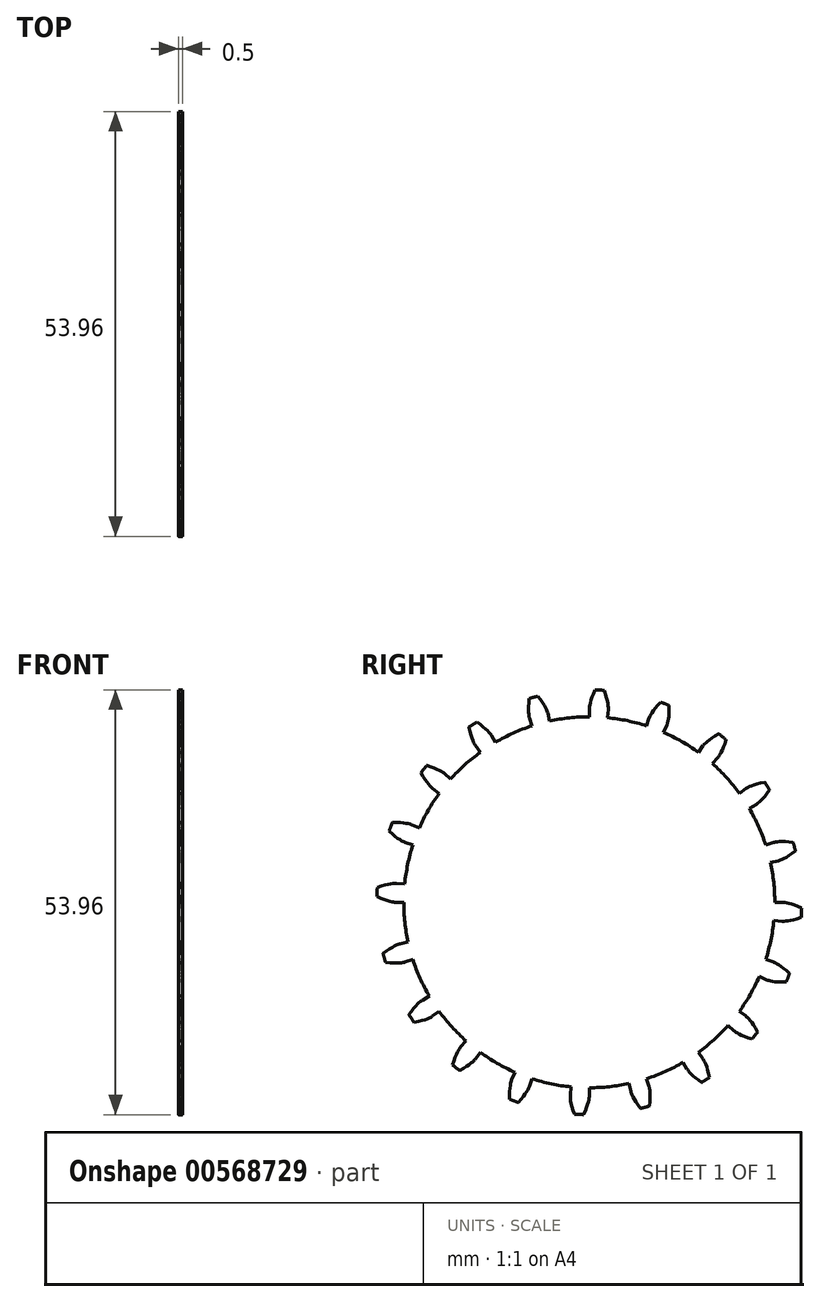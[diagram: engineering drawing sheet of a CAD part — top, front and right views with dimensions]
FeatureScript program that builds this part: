
annotation { "Feature Type Name" : "Feature", "Feature Type Description" : "" }
export const myFeature = defineFeature(function(context is Context, id is Id, definition is map)
    precondition{}
    {
        {
            assignVariable(context, id + "F0", {"name" : "GearThickness", "anyValue" : .5});
        }
        {
            var Q0;
            Q0=qCreatedBy(makeId("Right.planeOp"),FACE);
            var sketch = newSketch(context, id + "F1", { "sketchPlane" : qUnion([Q0])});
            skCircle(sketch, "E0", {"center": v(0, 0) * mm, "radius": 23.56 * mm});
            skCircle(sketch, "E1", {"center": v(0, 0) * mm, "radius": 24.6 * mm, "construction": true});
            skCircle(sketch, "E2", {"center": v(0, 0) * mm, "radius": 25.4 * mm, "construction": true});
            skCircle(sketch, "E3", {"center": v(0, 0) * mm, "radius": 26.99 * mm});
            skLineSegment(sketch, "E4", {"start": v(0, 0) * mm, "end": v(-24.6, 0) * mm, "construction": true});
            skLineSegment(sketch, "E5.1.0", {"start": v(0, 0) * mm, "end": v(-24.56, 1.23) * mm, "construction": true});
            skLineSegment(sketch, "E5.2.0", {"start": v(0, 0) * mm, "end": v(-24.47, 2.45) * mm, "construction": true});
            skLineSegment(sketch, "E5.3.0", {"start": v(0, 0) * mm, "end": v(-24.31, 3.67) * mm, "construction": true});
            skLineSegment(sketch, "E5.4.0", {"start": v(0, 0) * mm, "end": v(-24.1, 4.89) * mm, "construction": true});
            skLineSegment(sketch, "E5.5.0", {"start": v(0, 0) * mm, "end": v(-23.83, 6.08) * mm, "construction": true});
            skLineSegment(sketch, "E5.6.0", {"start": v(0, 0) * mm, "end": v(-23.5, 7.27) * mm, "construction": true});
            skLineSegment(sketch, "E5.7.0", {"start": v(0, 0) * mm, "end": v(-23.1, 8.43) * mm, "construction": true});
            skLineSegment(sketch, "E5.8.0", {"start": v(0, 0) * mm, "end": v(-22.65, 9.58) * mm, "construction": true});
            skLineSegment(sketch, "E5.9.0", {"start": v(0, 0) * mm, "end": v(-22.14, 10.7) * mm, "construction": true});
            skLineSegment(sketch, "E5.10.0", {"start": v(0, 0) * mm, "end": v(-21.58, 11.79) * mm, "construction": true});
            skLineSegment(sketch, "E5.11.0", {"start": v(0, 0) * mm, "end": v(-20.96, 12.85) * mm, "construction": true});
            skLineSegment(sketch, "E5.12.0", {"start": v(0, 0) * mm, "end": v(-20.3, 13.89) * mm, "construction": true});
            skLineSegment(sketch, "E5.13.0", {"start": v(0, 0) * mm, "end": v(-19.58, 14.88) * mm, "construction": true});
            skLineSegment(sketch, "E5.14.0", {"start": v(0, 0) * mm, "end": v(-18.8, 15.84) * mm, "construction": true});
            skLineSegment(sketch, "E5.anchor2", {"start": v(0, 0) * mm, "end": v(-18.8, 15.84) * mm, "construction": true});
            skLineSegment(sketch, "E6", {"start": v(-24.56, 1.23) * mm, "end": v(-24.62, 0) * mm, "construction": true});
            skLineSegment(sketch, "E7", {"start": v(-24.47, 2.45) * mm, "end": v(-24.71, 0) * mm, "construction": true});
            skLineSegment(sketch, "E8", {"start": v(-24.31, 3.67) * mm, "end": v(-24.87, 0.03) * mm, "construction": true});
            skLineSegment(sketch, "E9", {"start": v(-23.83, 6.08) * mm, "end": v(-25.35, 0.13) * mm, "construction": true});
            skLineSegment(sketch, "E10", {"start": v(-23.5, 7.27) * mm, "end": v(-25.67, 0.22) * mm, "construction": true});
            skLineSegment(sketch, "E11", {"start": v(-23.1, 8.43) * mm, "end": v(-26.05, 0.35) * mm, "construction": true});
            skLineSegment(sketch, "E12", {"start": v(-22.65, 9.58) * mm, "end": v(-26.48, 0.52) * mm, "construction": true});
            skLineSegment(sketch, "E13", {"start": v(-22.14, 10.7) * mm, "end": v(-26.96, 0.73) * mm, "construction": true});
            skLineSegment(sketch, "E14", {"start": v(-21.58, 11.79) * mm, "end": v(-27.48, 1) * mm, "construction": true});
            skLineSegment(sketch, "E15", {"start": v(-20.96, 12.85) * mm, "end": v(-28.03, 1.32) * mm, "construction": true});
            skLineSegment(sketch, "E16", {"start": v(-24.1, 4.89) * mm, "end": v(-25.08, 0.07) * mm, "construction": true});
            skLineSegment(sketch, "E17", {"start": v(-20.3, 13.89) * mm, "end": v(-28.63, 1.7) * mm, "construction": true});
            skLineSegment(sketch, "E18", {"start": v(-19.58, 14.88) * mm, "end": v(-29.25, 2.16) * mm, "construction": true});
            skLineSegment(sketch, "E19", {"start": v(-18.8, 15.84) * mm, "end": v(-29.9, 2.68) * mm, "construction": true});
            skLineSegment(sketch, "E20", {"start": v(0, 0) * mm, "end": v(-24.56, 1.2) * mm, "construction": true});
            skLineSegment(sketch, "E21", {"start": v(-23.56, 0) * mm, "end": v(-24.6, 0) * mm});
            skLineSegment(sketch, "E22.MirrorCS", {"start": v(-23.45, 2.3) * mm, "end": v(-24.47, 2.41) * mm});
            skLineSegment(sketch, "E23", {"start": v(-24.6, 0) * mm, "end": v(-24.62, 0) * mm});
            skLineSegment(sketch, "E24", {"start": v(-24.62, 0) * mm, "end": v(-24.71, 0) * mm});
            skLineSegment(sketch, "E25", {"start": v(-24.71, 0) * mm, "end": v(-24.87, 0.03) * mm});
            skLineSegment(sketch, "E26", {"start": v(-24.87, 0.03) * mm, "end": v(-25.08, 0.07) * mm});
            skLineSegment(sketch, "E27", {"start": v(-25.08, 0.07) * mm, "end": v(-25.35, 0.13) * mm});
            skLineSegment(sketch, "E28", {"start": v(-25.35, 0.13) * mm, "end": v(-25.67, 0.22) * mm});
            skLineSegment(sketch, "E29", {"start": v(-25.67, 0.22) * mm, "end": v(-26.05, 0.35) * mm});
            skLineSegment(sketch, "E30", {"start": v(-26.05, 0.35) * mm, "end": v(-26.48, 0.52) * mm});
            skLineSegment(sketch, "E31", {"start": v(-26.48, 0.52) * mm, "end": v(-26.96, 0.73) * mm});
            skLineSegment(sketch, "E32", {"start": v(-26.96, 0.73) * mm, "end": v(-27.48, 1) * mm});
            skLineSegment(sketch, "E33", {"start": v(-27.48, 1) * mm, "end": v(-28.03, 1.32) * mm});
            skLineSegment(sketch, "E34", {"start": v(-28.03, 1.32) * mm, "end": v(-28.63, 1.7) * mm});
            skLineSegment(sketch, "E35", {"start": v(-28.63, 1.7) * mm, "end": v(-29.25, 2.16) * mm});
            skLineSegment(sketch, "E36", {"start": v(-29.25, 2.16) * mm, "end": v(-29.9, 2.68) * mm});
            skLineSegment(sketch, "E37.MirrorCS", {"start": v(-24.47, 2.41) * mm, "end": v(-24.5, 2.41) * mm});
            skLineSegment(sketch, "E38.MirrorCS", {"start": v(-24.5, 2.41) * mm, "end": v(-24.6, 2.41) * mm});
            skLineSegment(sketch, "E39.MirrorCS", {"start": v(-24.6, 2.41) * mm, "end": v(-24.75, 2.4) * mm});
            skLineSegment(sketch, "E40.MirrorCS", {"start": v(-24.75, 2.4) * mm, "end": v(-24.96, 2.4) * mm});
            skLineSegment(sketch, "E41.MirrorCS", {"start": v(-25.24, 2.36) * mm, "end": v(-25.57, 2.3) * mm});
            skLineSegment(sketch, "E42.MirrorCS", {"start": v(-25.57, 2.3) * mm, "end": v(-25.96, 2.2) * mm});
            skLineSegment(sketch, "E43.MirrorCS", {"start": v(-25.96, 2.2) * mm, "end": v(-26.4, 2.08) * mm});
            skLineSegment(sketch, "E44.MirrorCS", {"start": v(-26.4, 2.08) * mm, "end": v(-26.9, 1.91) * mm});
            skLineSegment(sketch, "E45.MirrorCS", {"start": v(-27.44, 1.7) * mm, "end": v(-28.03, 1.43) * mm});
            skLineSegment(sketch, "E46.MirrorCS", {"start": v(-26.9, 1.91) * mm, "end": v(-27.44, 1.7) * mm});
            skLineSegment(sketch, "E47.MirrorCS", {"start": v(-28.03, 1.43) * mm, "end": v(-28.66, 1.1) * mm});
            skLineSegment(sketch, "E48.MirrorCS", {"start": v(-28.66, 1.1) * mm, "end": v(-29.32, 0.72) * mm});
            skLineSegment(sketch, "E49.MirrorCS", {"start": v(-29.32, 0.72) * mm, "end": v(-30.02, 0.27) * mm});
            skLineSegment(sketch, "E50.MirrorCS", {"start": v(-24.96, 2.4) * mm, "end": v(-25.24, 2.36) * mm});
            skLineSegment(sketch, "E51.1.0", {"start": v(-22.4, -7.28) * mm, "end": v(-23.39, -7.6) * mm});
            skLineSegment(sketch, "E51.1.1", {"start": v(-27.1, -7.3) * mm, "end": v(-27.6, -7.8) * mm});
            skLineSegment(sketch, "E51.1.2", {"start": v(-23.02, -5.05) * mm, "end": v(-24.02, -5.27) * mm});
            skLineSegment(sketch, "E51.1.3", {"start": v(-26.62, -6.86) * mm, "end": v(-27.1, -7.3) * mm});
            skLineSegment(sketch, "E51.1.4", {"start": v(-26.44, -7.54) * mm, "end": v(-27.07, -7.4) * mm});
            skLineSegment(sketch, "E51.1.5", {"start": v(-27.07, -7.4) * mm, "end": v(-27.75, -7.22) * mm});
            skLineSegment(sketch, "E51.1.6", {"start": v(-26.17, -6.5) * mm, "end": v(-26.62, -6.86) * mm});
            skLineSegment(sketch, "E51.1.7", {"start": v(-28.1, -8.38) * mm, "end": v(-28.63, -9.02) * mm});
            skLineSegment(sketch, "E51.1.8", {"start": v(-25.75, -6.18) * mm, "end": v(-26.17, -6.5) * mm});
            skLineSegment(sketch, "E51.1.9", {"start": v(-28.48, -6.99) * mm, "end": v(-29.26, -6.7) * mm});
            skLineSegment(sketch, "E51.1.10", {"start": v(-27.6, -7.8) * mm, "end": v(-28.1, -8.38) * mm});
            skLineSegment(sketch, "E51.1.11", {"start": v(-25.86, -7.63) * mm, "end": v(-26.44, -7.54) * mm});
            skLineSegment(sketch, "E51.1.12", {"start": v(-27.75, -7.22) * mm, "end": v(-28.48, -6.99) * mm});
            skLineSegment(sketch, "E51.1.13", {"start": v(-24.73, -5.56) * mm, "end": v(-25.03, -5.72) * mm});
            skLineSegment(sketch, "E51.1.14", {"start": v(-25.03, -5.72) * mm, "end": v(-25.37, -5.92) * mm});
            skLineSegment(sketch, "E51.1.15", {"start": v(-25.37, -5.92) * mm, "end": v(-25.75, -6.18) * mm});
            skLineSegment(sketch, "E51.1.16", {"start": v(-24.88, -7.72) * mm, "end": v(-25.34, -7.7) * mm});
            skLineSegment(sketch, "E51.1.17", {"start": v(-24.48, -7.72) * mm, "end": v(-24.88, -7.72) * mm});
            skLineSegment(sketch, "E51.1.18", {"start": v(-25.34, -7.7) * mm, "end": v(-25.86, -7.63) * mm});
            skLineSegment(sketch, "E51.1.19", {"start": v(-24.48, -5.44) * mm, "end": v(-24.73, -5.56) * mm});
            skLineSegment(sketch, "E51.1.20", {"start": v(-24.28, -5.36) * mm, "end": v(-24.48, -5.44) * mm});
            skLineSegment(sketch, "E51.1.21", {"start": v(-24.15, -7.71) * mm, "end": v(-24.48, -7.72) * mm});
            skLineSegment(sketch, "E51.1.22", {"start": v(-23.87, -7.69) * mm, "end": v(-24.15, -7.71) * mm});
            skLineSegment(sketch, "E51.1.23", {"start": v(-23.5, -7.63) * mm, "end": v(-23.66, -7.66) * mm});
            skLineSegment(sketch, "E51.1.24", {"start": v(-24.02, -5.27) * mm, "end": v(-24.05, -5.28) * mm});
            skLineSegment(sketch, "E51.1.25", {"start": v(-24.05, -5.28) * mm, "end": v(-24.14, -5.3) * mm});
            skLineSegment(sketch, "E51.1.26", {"start": v(-23.66, -7.66) * mm, "end": v(-23.87, -7.69) * mm});
            skLineSegment(sketch, "E51.1.27", {"start": v(-24.14, -5.3) * mm, "end": v(-24.28, -5.36) * mm});
            skLineSegment(sketch, "E51.1.28", {"start": v(-23.42, -7.6) * mm, "end": v(-23.5, -7.63) * mm});
            skLineSegment(sketch, "E51.1.29", {"start": v(-23.39, -7.6) * mm, "end": v(-23.42, -7.6) * mm});
            skLineSegment(sketch, "E51.2.0", {"start": v(-19.06, -13.85) * mm, "end": v(-19.9, -14.45) * mm});
            skLineSegment(sketch, "E51.2.1", {"start": v(-23.52, -15.32) * mm, "end": v(-23.83, -15.95) * mm});
            skLineSegment(sketch, "E51.2.2", {"start": v(-20.33, -11.91) * mm, "end": v(-21.22, -12.43) * mm});
            skLineSegment(sketch, "E51.2.3", {"start": v(-23.2, -14.76) * mm, "end": v(-23.52, -15.32) * mm});
            skLineSegment(sketch, "E51.2.4", {"start": v(-22.82, -15.34) * mm, "end": v(-23.46, -15.4) * mm});
            skLineSegment(sketch, "E51.2.5", {"start": v(-23.46, -15.4) * mm, "end": v(-24.16, -15.44) * mm});
            skLineSegment(sketch, "E51.2.6", {"start": v(-22.89, -14.26) * mm, "end": v(-23.2, -14.76) * mm});
            skLineSegment(sketch, "E51.2.7", {"start": v(-24.14, -16.65) * mm, "end": v(-24.44, -17.43) * mm});
            skLineSegment(sketch, "E51.2.8", {"start": v(-22.58, -13.84) * mm, "end": v(-22.89, -14.26) * mm});
            skLineSegment(sketch, "E51.2.9", {"start": v(-24.93, -15.45) * mm, "end": v(-25.76, -15.4) * mm});
            skLineSegment(sketch, "E51.2.10", {"start": v(-23.83, -15.95) * mm, "end": v(-24.14, -16.65) * mm});
            skLineSegment(sketch, "E51.2.11", {"start": v(-22.24, -15.25) * mm, "end": v(-22.82, -15.34) * mm});
            skLineSegment(sketch, "E51.2.12", {"start": v(-24.16, -15.44) * mm, "end": v(-24.93, -15.45) * mm});
            skLineSegment(sketch, "E51.2.13", {"start": v(-21.8, -12.93) * mm, "end": v(-22.04, -13.17) * mm});
            skLineSegment(sketch, "E51.2.14", {"start": v(-22.04, -13.17) * mm, "end": v(-22.3, -13.47) * mm});
            skLineSegment(sketch, "E51.2.15", {"start": v(-22.3, -13.47) * mm, "end": v(-22.58, -13.84) * mm});
            skLineSegment(sketch, "E51.2.16", {"start": v(-21.28, -15.03) * mm, "end": v(-21.73, -15.15) * mm});
            skLineSegment(sketch, "E51.2.17", {"start": v(-20.9, -14.91) * mm, "end": v(-21.28, -15.03) * mm});
            skLineSegment(sketch, "E51.2.18", {"start": v(-21.73, -15.15) * mm, "end": v(-22.24, -15.25) * mm});
            skLineSegment(sketch, "E51.2.19", {"start": v(-21.6, -12.74) * mm, "end": v(-21.8, -12.93) * mm});
            skLineSegment(sketch, "E51.2.20", {"start": v(-21.44, -12.6) * mm, "end": v(-21.6, -12.74) * mm});
            skLineSegment(sketch, "E51.2.21", {"start": v(-20.58, -14.8) * mm, "end": v(-20.9, -14.91) * mm});
            skLineSegment(sketch, "E51.2.22", {"start": v(-20.33, -14.69) * mm, "end": v(-20.58, -14.8) * mm});
            skLineSegment(sketch, "E51.2.23", {"start": v(-20, -14.52) * mm, "end": v(-20.13, -14.6) * mm});
            skLineSegment(sketch, "E51.2.24", {"start": v(-21.22, -12.43) * mm, "end": v(-21.24, -12.45) * mm});
            skLineSegment(sketch, "E51.2.25", {"start": v(-21.24, -12.45) * mm, "end": v(-21.32, -12.5) * mm});
            skLineSegment(sketch, "E51.2.26", {"start": v(-20.13, -14.6) * mm, "end": v(-20.33, -14.69) * mm});
            skLineSegment(sketch, "E51.2.27", {"start": v(-21.32, -12.5) * mm, "end": v(-21.44, -12.6) * mm});
            skLineSegment(sketch, "E51.2.28", {"start": v(-19.92, -14.47) * mm, "end": v(-20, -14.52) * mm});
            skLineSegment(sketch, "E51.2.29", {"start": v(-19.9, -14.45) * mm, "end": v(-19.92, -14.47) * mm});
            skLineSegment(sketch, "E51.3.0", {"start": v(-13.85, -19.06) * mm, "end": v(-14.45, -19.9) * mm});
            skLineSegment(sketch, "E51.3.1", {"start": v(-17.63, -21.83) * mm, "end": v(-17.74, -22.53) * mm});
            skLineSegment(sketch, "E51.3.2", {"start": v(-15.65, -17.61) * mm, "end": v(-16.33, -18.38) * mm});
            skLineSegment(sketch, "E51.3.3", {"start": v(-17.5, -21.2) * mm, "end": v(-17.63, -21.83) * mm});
            skLineSegment(sketch, "E51.3.4", {"start": v(-16.96, -21.64) * mm, "end": v(-17.55, -21.9) * mm});
            skLineSegment(sketch, "E51.3.5", {"start": v(-17.55, -21.9) * mm, "end": v(-18.2, -22.16) * mm});
            skLineSegment(sketch, "E51.3.6", {"start": v(-17.36, -20.64) * mm, "end": v(-17.5, -21.2) * mm});
            skLineSegment(sketch, "E51.3.7", {"start": v(-17.82, -23.3) * mm, "end": v(-17.86, -24.13) * mm});
            skLineSegment(sketch, "E51.3.8", {"start": v(-17.2, -20.14) * mm, "end": v(-17.36, -20.64) * mm});
            skLineSegment(sketch, "E51.3.9", {"start": v(-18.94, -22.4) * mm, "end": v(-19.74, -22.61) * mm});
            skLineSegment(sketch, "E51.3.10", {"start": v(-17.74, -22.53) * mm, "end": v(-17.82, -23.3) * mm});
            skLineSegment(sketch, "E51.3.11", {"start": v(-16.44, -21.38) * mm, "end": v(-16.96, -21.64) * mm});
            skLineSegment(sketch, "E51.3.12", {"start": v(-18.2, -22.16) * mm, "end": v(-18.94, -22.4) * mm});
            skLineSegment(sketch, "E51.3.13", {"start": v(-16.74, -19.03) * mm, "end": v(-16.89, -19.34) * mm});
            skLineSegment(sketch, "E51.3.14", {"start": v(-16.89, -19.34) * mm, "end": v(-17.05, -19.7) * mm});
            skLineSegment(sketch, "E51.3.15", {"start": v(-17.05, -19.7) * mm, "end": v(-17.2, -20.14) * mm});
            skLineSegment(sketch, "E51.3.16", {"start": v(-15.6, -20.87) * mm, "end": v(-15.98, -21.12) * mm});
            skLineSegment(sketch, "E51.3.17", {"start": v(-15.27, -20.64) * mm, "end": v(-15.6, -20.87) * mm});
            skLineSegment(sketch, "E51.3.18", {"start": v(-15.98, -21.12) * mm, "end": v(-16.44, -21.38) * mm});
            skLineSegment(sketch, "E51.3.19", {"start": v(-16.6, -18.79) * mm, "end": v(-16.74, -19.03) * mm});
            skLineSegment(sketch, "E51.3.20", {"start": v(-16.5, -18.6) * mm, "end": v(-16.6, -18.79) * mm});
            skLineSegment(sketch, "E51.3.21", {"start": v(-15, -20.43) * mm, "end": v(-15.27, -20.64) * mm});
            skLineSegment(sketch, "E51.3.22", {"start": v(-14.8, -20.25) * mm, "end": v(-15, -20.43) * mm});
            skLineSegment(sketch, "E51.3.23", {"start": v(-14.53, -19.99) * mm, "end": v(-14.64, -20.1) * mm});
            skLineSegment(sketch, "E51.3.24", {"start": v(-16.33, -18.38) * mm, "end": v(-16.35, -18.4) * mm});
            skLineSegment(sketch, "E51.3.25", {"start": v(-16.35, -18.4) * mm, "end": v(-16.4, -18.48) * mm});
            skLineSegment(sketch, "E51.3.26", {"start": v(-14.64, -20.1) * mm, "end": v(-14.8, -20.25) * mm});
            skLineSegment(sketch, "E51.3.27", {"start": v(-16.4, -18.48) * mm, "end": v(-16.5, -18.6) * mm});
            skLineSegment(sketch, "E51.3.28", {"start": v(-14.47, -19.92) * mm, "end": v(-14.53, -19.99) * mm});
            skLineSegment(sketch, "E51.3.29", {"start": v(-14.45, -19.9) * mm, "end": v(-14.47, -19.92) * mm});
            skLineSegment(sketch, "E51.4.0", {"start": v(-7.28, -22.4) * mm, "end": v(-7.6, -23.39) * mm});
            skLineSegment(sketch, "E51.4.1", {"start": v(-10.02, -26.21) * mm, "end": v(-9.9, -26.91) * mm});
            skLineSegment(sketch, "E51.4.2", {"start": v(-9.44, -21.59) * mm, "end": v(-9.85, -22.53) * mm});
            skLineSegment(sketch, "E51.4.3", {"start": v(-10.1, -25.57) * mm, "end": v(-10.02, -26.21) * mm});
            skLineSegment(sketch, "E51.4.4", {"start": v(-9.44, -25.82) * mm, "end": v(-9.92, -26.25) * mm});
            skLineSegment(sketch, "E51.4.5", {"start": v(-9.92, -26.25) * mm, "end": v(-10.47, -26.7) * mm});
            skLineSegment(sketch, "E51.4.6", {"start": v(-10.13, -25) * mm, "end": v(-10.1, -25.57) * mm});
            skLineSegment(sketch, "E51.4.7", {"start": v(-9.75, -27.66) * mm, "end": v(-9.53, -28.46) * mm});
            skLineSegment(sketch, "E51.4.8", {"start": v(-10.14, -24.47) * mm, "end": v(-10.13, -25) * mm});
            skLineSegment(sketch, "E51.4.9", {"start": v(-11.1, -27.15) * mm, "end": v(-11.78, -27.6) * mm});
            skLineSegment(sketch, "E51.4.10", {"start": v(-9.9, -26.91) * mm, "end": v(-9.75, -27.66) * mm});
            skLineSegment(sketch, "E51.4.11", {"start": v(-9.03, -25.41) * mm, "end": v(-9.44, -25.82) * mm});
            skLineSegment(sketch, "E51.4.12", {"start": v(-10.47, -26.7) * mm, "end": v(-11.1, -27.15) * mm});
            skLineSegment(sketch, "E51.4.13", {"start": v(-10.04, -23.27) * mm, "end": v(-10.09, -23.6) * mm});
            skLineSegment(sketch, "E51.4.14", {"start": v(-10.09, -23.6) * mm, "end": v(-10.12, -24) * mm});
            skLineSegment(sketch, "E51.4.15", {"start": v(-10.12, -24) * mm, "end": v(-10.14, -24.47) * mm});
            skLineSegment(sketch, "E51.4.16", {"start": v(-8.38, -24.67) * mm, "end": v(-8.67, -25.02) * mm});
            skLineSegment(sketch, "E51.4.17", {"start": v(-8.14, -24.35) * mm, "end": v(-8.38, -24.67) * mm});
            skLineSegment(sketch, "E51.4.18", {"start": v(-8.67, -25.02) * mm, "end": v(-9.03, -25.41) * mm});
            skLineSegment(sketch, "E51.4.19", {"start": v(-10, -23) * mm, "end": v(-10.04, -23.27) * mm});
            skLineSegment(sketch, "E51.4.20", {"start": v(-9.94, -22.8) * mm, "end": v(-10, -23) * mm});
            skLineSegment(sketch, "E51.4.21", {"start": v(-7.95, -24.07) * mm, "end": v(-8.14, -24.35) * mm});
            skLineSegment(sketch, "E51.4.22", {"start": v(-7.81, -23.83) * mm, "end": v(-7.95, -24.07) * mm});
            skLineSegment(sketch, "E51.4.23", {"start": v(-7.64, -23.5) * mm, "end": v(-7.71, -23.64) * mm});
            skLineSegment(sketch, "E51.4.24", {"start": v(-9.85, -22.53) * mm, "end": v(-9.87, -22.56) * mm});
            skLineSegment(sketch, "E51.4.25", {"start": v(-9.87, -22.56) * mm, "end": v(-9.9, -22.65) * mm});
            skLineSegment(sketch, "E51.4.26", {"start": v(-7.71, -23.64) * mm, "end": v(-7.81, -23.83) * mm});
            skLineSegment(sketch, "E51.4.27", {"start": v(-9.9, -22.65) * mm, "end": v(-9.94, -22.8) * mm});
            skLineSegment(sketch, "E51.4.28", {"start": v(-7.6, -23.42) * mm, "end": v(-7.64, -23.5) * mm});
            skLineSegment(sketch, "E51.4.29", {"start": v(-7.6, -23.39) * mm, "end": v(-7.6, -23.42) * mm});
            skLineSegment(sketch, "E51.5.0", {"start": v(0, -23.56) * mm, "end": v(0, -24.6) * mm});
            skLineSegment(sketch, "E51.5.1", {"start": v(-1.43, -28.03) * mm, "end": v(-1.1, -28.66) * mm});
            skLineSegment(sketch, "E51.5.2", {"start": v(-2.3, -23.45) * mm, "end": v(-2.41, -24.47) * mm});
            skLineSegment(sketch, "E51.5.3", {"start": v(-1.7, -27.44) * mm, "end": v(-1.43, -28.03) * mm});
            skLineSegment(sketch, "E51.5.4", {"start": v(-1, -27.48) * mm, "end": v(-1.32, -28.03) * mm});
            skLineSegment(sketch, "E51.5.5", {"start": v(-1.32, -28.03) * mm, "end": v(-1.7, -28.63) * mm});
            skLineSegment(sketch, "E51.5.6", {"start": v(-1.91, -26.9) * mm, "end": v(-1.7, -27.44) * mm});
            skLineSegment(sketch, "E51.5.7", {"start": v(-0.72, -29.32) * mm, "end": v(-0.27, -30.02) * mm});
            skLineSegment(sketch, "E51.5.8", {"start": v(-2.08, -26.4) * mm, "end": v(-1.91, -26.9) * mm});
            skLineSegment(sketch, "E51.5.9", {"start": v(-2.16, -29.25) * mm, "end": v(-2.68, -29.9) * mm});
            skLineSegment(sketch, "E51.5.10", {"start": v(-1.1, -28.66) * mm, "end": v(-0.72, -29.32) * mm});
            skLineSegment(sketch, "E51.5.11", {"start": v(-0.73, -26.96) * mm, "end": v(-1, -27.48) * mm});
            skLineSegment(sketch, "E51.5.12", {"start": v(-1.7, -28.63) * mm, "end": v(-2.16, -29.25) * mm});
            skLineSegment(sketch, "E51.5.13", {"start": v(-2.36, -25.24) * mm, "end": v(-2.3, -25.57) * mm});
            skLineSegment(sketch, "E51.5.14", {"start": v(-2.3, -25.57) * mm, "end": v(-2.2, -25.96) * mm});
            skLineSegment(sketch, "E51.5.15", {"start": v(-2.2, -25.96) * mm, "end": v(-2.08, -26.4) * mm});
            skLineSegment(sketch, "E51.5.16", {"start": v(-0.35, -26.05) * mm, "end": v(-0.52, -26.48) * mm});
            skLineSegment(sketch, "E51.5.17", {"start": v(-0.22, -25.67) * mm, "end": v(-0.35, -26.05) * mm});
            skLineSegment(sketch, "E51.5.18", {"start": v(-0.52, -26.48) * mm, "end": v(-0.73, -26.96) * mm});
            skLineSegment(sketch, "E51.5.19", {"start": v(-2.4, -24.96) * mm, "end": v(-2.36, -25.24) * mm});
            skLineSegment(sketch, "E51.5.20", {"start": v(-2.4, -24.75) * mm, "end": v(-2.4, -24.96) * mm});
            skLineSegment(sketch, "E51.5.21", {"start": v(-0.13, -25.35) * mm, "end": v(-0.22, -25.67) * mm});
            skLineSegment(sketch, "E51.5.22", {"start": v(-0.07, -25.08) * mm, "end": v(-0.13, -25.35) * mm});
            skLineSegment(sketch, "E51.5.23", {"start": v(0, -24.71) * mm, "end": v(-0.03, -24.87) * mm});
            skLineSegment(sketch, "E51.5.24", {"start": v(-2.41, -24.47) * mm, "end": v(-2.41, -24.5) * mm});
            skLineSegment(sketch, "E51.5.25", {"start": v(-2.41, -24.5) * mm, "end": v(-2.41, -24.6) * mm});
            skLineSegment(sketch, "E51.5.26", {"start": v(-0.03, -24.87) * mm, "end": v(-0.07, -25.08) * mm});
            skLineSegment(sketch, "E51.5.27", {"start": v(-2.41, -24.6) * mm, "end": v(-2.4, -24.75) * mm});
            skLineSegment(sketch, "E51.5.28", {"start": v(0, -24.62) * mm, "end": v(0, -24.71) * mm});
            skLineSegment(sketch, "E51.5.29", {"start": v(0, -24.6) * mm, "end": v(0, -24.62) * mm});
            skLineSegment(sketch, "E51.6.0", {"start": v(7.28, -22.4) * mm, "end": v(7.6, -23.39) * mm});
            skLineSegment(sketch, "E51.6.1", {"start": v(7.3, -27.1) * mm, "end": v(7.8, -27.6) * mm});
            skLineSegment(sketch, "E51.6.2", {"start": v(5.05, -23.02) * mm, "end": v(5.27, -24.02) * mm});
            skLineSegment(sketch, "E51.6.3", {"start": v(6.86, -26.62) * mm, "end": v(7.3, -27.1) * mm});
            skLineSegment(sketch, "E51.6.4", {"start": v(7.54, -26.44) * mm, "end": v(7.4, -27.07) * mm});
            skLineSegment(sketch, "E51.6.5", {"start": v(7.4, -27.07) * mm, "end": v(7.22, -27.75) * mm});
            skLineSegment(sketch, "E51.6.6", {"start": v(6.5, -26.17) * mm, "end": v(6.86, -26.62) * mm});
            skLineSegment(sketch, "E51.6.7", {"start": v(8.38, -28.1) * mm, "end": v(9.02, -28.63) * mm});
            skLineSegment(sketch, "E51.6.8", {"start": v(6.18, -25.75) * mm, "end": v(6.5, -26.17) * mm});
            skLineSegment(sketch, "E51.6.9", {"start": v(6.99, -28.48) * mm, "end": v(6.7, -29.26) * mm});
            skLineSegment(sketch, "E51.6.10", {"start": v(7.8, -27.6) * mm, "end": v(8.38, -28.1) * mm});
            skLineSegment(sketch, "E51.6.11", {"start": v(7.63, -25.86) * mm, "end": v(7.54, -26.44) * mm});
            skLineSegment(sketch, "E51.6.12", {"start": v(7.22, -27.75) * mm, "end": v(6.99, -28.48) * mm});
            skLineSegment(sketch, "E51.6.13", {"start": v(5.56, -24.73) * mm, "end": v(5.72, -25.03) * mm});
            skLineSegment(sketch, "E51.6.14", {"start": v(5.72, -25.03) * mm, "end": v(5.92, -25.37) * mm});
            skLineSegment(sketch, "E51.6.15", {"start": v(5.92, -25.37) * mm, "end": v(6.18, -25.75) * mm});
            skLineSegment(sketch, "E51.6.16", {"start": v(7.72, -24.88) * mm, "end": v(7.7, -25.34) * mm});
            skLineSegment(sketch, "E51.6.17", {"start": v(7.72, -24.48) * mm, "end": v(7.72, -24.88) * mm});
            skLineSegment(sketch, "E51.6.18", {"start": v(7.7, -25.34) * mm, "end": v(7.63, -25.86) * mm});
            skLineSegment(sketch, "E51.6.19", {"start": v(5.44, -24.48) * mm, "end": v(5.56, -24.73) * mm});
            skLineSegment(sketch, "E51.6.20", {"start": v(5.36, -24.28) * mm, "end": v(5.44, -24.48) * mm});
            skLineSegment(sketch, "E51.6.21", {"start": v(7.71, -24.15) * mm, "end": v(7.72, -24.48) * mm});
            skLineSegment(sketch, "E51.6.22", {"start": v(7.69, -23.87) * mm, "end": v(7.71, -24.15) * mm});
            skLineSegment(sketch, "E51.6.23", {"start": v(7.63, -23.5) * mm, "end": v(7.66, -23.66) * mm});
            skLineSegment(sketch, "E51.6.24", {"start": v(5.27, -24.02) * mm, "end": v(5.28, -24.05) * mm});
            skLineSegment(sketch, "E51.6.25", {"start": v(5.28, -24.05) * mm, "end": v(5.3, -24.14) * mm});
            skLineSegment(sketch, "E51.6.26", {"start": v(7.66, -23.66) * mm, "end": v(7.69, -23.87) * mm});
            skLineSegment(sketch, "E51.6.27", {"start": v(5.3, -24.14) * mm, "end": v(5.36, -24.28) * mm});
            skLineSegment(sketch, "E51.6.28", {"start": v(7.6, -23.42) * mm, "end": v(7.63, -23.5) * mm});
            skLineSegment(sketch, "E51.6.29", {"start": v(7.6, -23.39) * mm, "end": v(7.6, -23.42) * mm});
            skLineSegment(sketch, "E51.7.0", {"start": v(13.85, -19.06) * mm, "end": v(14.45, -19.9) * mm});
            skLineSegment(sketch, "E51.7.1", {"start": v(15.32, -23.52) * mm, "end": v(15.95, -23.83) * mm});
            skLineSegment(sketch, "E51.7.2", {"start": v(11.91, -20.33) * mm, "end": v(12.43, -21.22) * mm});
            skLineSegment(sketch, "E51.7.3", {"start": v(14.76, -23.2) * mm, "end": v(15.32, -23.52) * mm});
            skLineSegment(sketch, "E51.7.4", {"start": v(15.34, -22.82) * mm, "end": v(15.4, -23.46) * mm});
            skLineSegment(sketch, "E51.7.5", {"start": v(15.4, -23.46) * mm, "end": v(15.44, -24.16) * mm});
            skLineSegment(sketch, "E51.7.6", {"start": v(14.26, -22.89) * mm, "end": v(14.76, -23.2) * mm});
            skLineSegment(sketch, "E51.7.7", {"start": v(16.65, -24.14) * mm, "end": v(17.43, -24.44) * mm});
            skLineSegment(sketch, "E51.7.8", {"start": v(13.84, -22.58) * mm, "end": v(14.26, -22.89) * mm});
            skLineSegment(sketch, "E51.7.9", {"start": v(15.45, -24.93) * mm, "end": v(15.4, -25.76) * mm});
            skLineSegment(sketch, "E51.7.10", {"start": v(15.95, -23.83) * mm, "end": v(16.65, -24.14) * mm});
            skLineSegment(sketch, "E51.7.11", {"start": v(15.25, -22.24) * mm, "end": v(15.34, -22.82) * mm});
            skLineSegment(sketch, "E51.7.12", {"start": v(15.44, -24.16) * mm, "end": v(15.45, -24.93) * mm});
            skLineSegment(sketch, "E51.7.13", {"start": v(12.93, -21.8) * mm, "end": v(13.17, -22.04) * mm});
            skLineSegment(sketch, "E51.7.14", {"start": v(13.17, -22.04) * mm, "end": v(13.47, -22.3) * mm});
            skLineSegment(sketch, "E51.7.15", {"start": v(13.47, -22.3) * mm, "end": v(13.84, -22.58) * mm});
            skLineSegment(sketch, "E51.7.16", {"start": v(15.03, -21.28) * mm, "end": v(15.15, -21.73) * mm});
            skLineSegment(sketch, "E51.7.17", {"start": v(14.91, -20.9) * mm, "end": v(15.03, -21.28) * mm});
            skLineSegment(sketch, "E51.7.18", {"start": v(15.15, -21.73) * mm, "end": v(15.25, -22.24) * mm});
            skLineSegment(sketch, "E51.7.19", {"start": v(12.74, -21.6) * mm, "end": v(12.93, -21.8) * mm});
            skLineSegment(sketch, "E51.7.20", {"start": v(12.6, -21.44) * mm, "end": v(12.74, -21.6) * mm});
            skLineSegment(sketch, "E51.7.21", {"start": v(14.8, -20.58) * mm, "end": v(14.91, -20.9) * mm});
            skLineSegment(sketch, "E51.7.22", {"start": v(14.69, -20.33) * mm, "end": v(14.8, -20.58) * mm});
            skLineSegment(sketch, "E51.7.23", {"start": v(14.52, -20) * mm, "end": v(14.6, -20.13) * mm});
            skLineSegment(sketch, "E51.7.24", {"start": v(12.43, -21.22) * mm, "end": v(12.45, -21.24) * mm});
            skLineSegment(sketch, "E51.7.25", {"start": v(12.45, -21.24) * mm, "end": v(12.5, -21.32) * mm});
            skLineSegment(sketch, "E51.7.26", {"start": v(14.6, -20.13) * mm, "end": v(14.69, -20.33) * mm});
            skLineSegment(sketch, "E51.7.27", {"start": v(12.5, -21.32) * mm, "end": v(12.6, -21.44) * mm});
            skLineSegment(sketch, "E51.7.28", {"start": v(14.47, -19.92) * mm, "end": v(14.52, -20) * mm});
            skLineSegment(sketch, "E51.7.29", {"start": v(14.45, -19.9) * mm, "end": v(14.47, -19.92) * mm});
            skLineSegment(sketch, "E51.8.0", {"start": v(19.06, -13.85) * mm, "end": v(19.9, -14.45) * mm});
            skLineSegment(sketch, "E51.8.1", {"start": v(21.83, -17.63) * mm, "end": v(22.53, -17.74) * mm});
            skLineSegment(sketch, "E51.8.2", {"start": v(17.61, -15.65) * mm, "end": v(18.38, -16.33) * mm});
            skLineSegment(sketch, "E51.8.3", {"start": v(21.2, -17.5) * mm, "end": v(21.83, -17.63) * mm});
            skLineSegment(sketch, "E51.8.4", {"start": v(21.64, -16.96) * mm, "end": v(21.9, -17.55) * mm});
            skLineSegment(sketch, "E51.8.5", {"start": v(21.9, -17.55) * mm, "end": v(22.16, -18.2) * mm});
            skLineSegment(sketch, "E51.8.6", {"start": v(20.64, -17.36) * mm, "end": v(21.2, -17.5) * mm});
            skLineSegment(sketch, "E51.8.7", {"start": v(23.3, -17.82) * mm, "end": v(24.13, -17.86) * mm});
            skLineSegment(sketch, "E51.8.8", {"start": v(20.14, -17.2) * mm, "end": v(20.64, -17.36) * mm});
            skLineSegment(sketch, "E51.8.9", {"start": v(22.4, -18.94) * mm, "end": v(22.61, -19.74) * mm});
            skLineSegment(sketch, "E51.8.10", {"start": v(22.53, -17.74) * mm, "end": v(23.3, -17.82) * mm});
            skLineSegment(sketch, "E51.8.11", {"start": v(21.38, -16.44) * mm, "end": v(21.64, -16.96) * mm});
            skLineSegment(sketch, "E51.8.12", {"start": v(22.16, -18.2) * mm, "end": v(22.4, -18.94) * mm});
            skLineSegment(sketch, "E51.8.13", {"start": v(19.03, -16.74) * mm, "end": v(19.34, -16.89) * mm});
            skLineSegment(sketch, "E51.8.14", {"start": v(19.34, -16.89) * mm, "end": v(19.7, -17.05) * mm});
            skLineSegment(sketch, "E51.8.15", {"start": v(19.7, -17.05) * mm, "end": v(20.14, -17.2) * mm});
            skLineSegment(sketch, "E51.8.16", {"start": v(20.87, -15.6) * mm, "end": v(21.12, -15.98) * mm});
            skLineSegment(sketch, "E51.8.17", {"start": v(20.64, -15.27) * mm, "end": v(20.87, -15.6) * mm});
            skLineSegment(sketch, "E51.8.18", {"start": v(21.12, -15.98) * mm, "end": v(21.38, -16.44) * mm});
            skLineSegment(sketch, "E51.8.19", {"start": v(18.79, -16.6) * mm, "end": v(19.03, -16.74) * mm});
            skLineSegment(sketch, "E51.8.20", {"start": v(18.6, -16.5) * mm, "end": v(18.79, -16.6) * mm});
            skLineSegment(sketch, "E51.8.21", {"start": v(20.43, -15) * mm, "end": v(20.64, -15.27) * mm});
            skLineSegment(sketch, "E51.8.22", {"start": v(20.25, -14.8) * mm, "end": v(20.43, -15) * mm});
            skLineSegment(sketch, "E51.8.23", {"start": v(19.99, -14.53) * mm, "end": v(20.1, -14.64) * mm});
            skLineSegment(sketch, "E51.8.24", {"start": v(18.38, -16.33) * mm, "end": v(18.4, -16.35) * mm});
            skLineSegment(sketch, "E51.8.25", {"start": v(18.4, -16.35) * mm, "end": v(18.48, -16.4) * mm});
            skLineSegment(sketch, "E51.8.26", {"start": v(20.1, -14.64) * mm, "end": v(20.25, -14.8) * mm});
            skLineSegment(sketch, "E51.8.27", {"start": v(18.48, -16.4) * mm, "end": v(18.6, -16.5) * mm});
            skLineSegment(sketch, "E51.8.28", {"start": v(19.92, -14.47) * mm, "end": v(19.99, -14.53) * mm});
            skLineSegment(sketch, "E51.8.29", {"start": v(19.9, -14.45) * mm, "end": v(19.92, -14.47) * mm});
            skLineSegment(sketch, "E51.9.0", {"start": v(22.4, -7.28) * mm, "end": v(23.39, -7.6) * mm});
            skLineSegment(sketch, "E51.9.1", {"start": v(26.21, -10.02) * mm, "end": v(26.91, -9.9) * mm});
            skLineSegment(sketch, "E51.9.2", {"start": v(21.59, -9.44) * mm, "end": v(22.53, -9.85) * mm});
            skLineSegment(sketch, "E51.9.3", {"start": v(25.57, -10.1) * mm, "end": v(26.21, -10.02) * mm});
            skLineSegment(sketch, "E51.9.4", {"start": v(25.82, -9.44) * mm, "end": v(26.25, -9.92) * mm});
            skLineSegment(sketch, "E51.9.5", {"start": v(26.25, -9.92) * mm, "end": v(26.7, -10.47) * mm});
            skLineSegment(sketch, "E51.9.6", {"start": v(25, -10.13) * mm, "end": v(25.57, -10.1) * mm});
            skLineSegment(sketch, "E51.9.7", {"start": v(27.66, -9.75) * mm, "end": v(28.46, -9.53) * mm});
            skLineSegment(sketch, "E51.9.8", {"start": v(24.47, -10.14) * mm, "end": v(25, -10.13) * mm});
            skLineSegment(sketch, "E51.9.9", {"start": v(27.15, -11.1) * mm, "end": v(27.6, -11.78) * mm});
            skLineSegment(sketch, "E51.9.10", {"start": v(26.91, -9.9) * mm, "end": v(27.66, -9.75) * mm});
            skLineSegment(sketch, "E51.9.11", {"start": v(25.41, -9.03) * mm, "end": v(25.82, -9.44) * mm});
            skLineSegment(sketch, "E51.9.12", {"start": v(26.7, -10.47) * mm, "end": v(27.15, -11.1) * mm});
            skLineSegment(sketch, "E51.9.13", {"start": v(23.27, -10.04) * mm, "end": v(23.6, -10.09) * mm});
            skLineSegment(sketch, "E51.9.14", {"start": v(23.6, -10.09) * mm, "end": v(24, -10.12) * mm});
            skLineSegment(sketch, "E51.9.15", {"start": v(24, -10.12) * mm, "end": v(24.47, -10.14) * mm});
            skLineSegment(sketch, "E51.9.16", {"start": v(24.67, -8.38) * mm, "end": v(25.02, -8.67) * mm});
            skLineSegment(sketch, "E51.9.17", {"start": v(24.35, -8.14) * mm, "end": v(24.67, -8.38) * mm});
            skLineSegment(sketch, "E51.9.18", {"start": v(25.02, -8.67) * mm, "end": v(25.41, -9.03) * mm});
            skLineSegment(sketch, "E51.9.19", {"start": v(23, -10) * mm, "end": v(23.27, -10.04) * mm});
            skLineSegment(sketch, "E51.9.20", {"start": v(22.8, -9.94) * mm, "end": v(23, -10) * mm});
            skLineSegment(sketch, "E51.9.21", {"start": v(24.07, -7.95) * mm, "end": v(24.35, -8.14) * mm});
            skLineSegment(sketch, "E51.9.22", {"start": v(23.83, -7.81) * mm, "end": v(24.07, -7.95) * mm});
            skLineSegment(sketch, "E51.9.23", {"start": v(23.5, -7.64) * mm, "end": v(23.64, -7.71) * mm});
            skLineSegment(sketch, "E51.9.24", {"start": v(22.53, -9.85) * mm, "end": v(22.56, -9.87) * mm});
            skLineSegment(sketch, "E51.9.25", {"start": v(22.56, -9.87) * mm, "end": v(22.65, -9.9) * mm});
            skLineSegment(sketch, "E51.9.26", {"start": v(23.64, -7.71) * mm, "end": v(23.83, -7.81) * mm});
            skLineSegment(sketch, "E51.9.27", {"start": v(22.65, -9.9) * mm, "end": v(22.8, -9.94) * mm});
            skLineSegment(sketch, "E51.9.28", {"start": v(23.42, -7.6) * mm, "end": v(23.5, -7.64) * mm});
            skLineSegment(sketch, "E51.9.29", {"start": v(23.39, -7.6) * mm, "end": v(23.42, -7.6) * mm});
            skLineSegment(sketch, "E51.10.0", {"start": v(23.56, 0) * mm, "end": v(24.6, 0) * mm});
            skLineSegment(sketch, "E51.10.1", {"start": v(28.03, -1.43) * mm, "end": v(28.66, -1.1) * mm});
            skLineSegment(sketch, "E51.10.2", {"start": v(23.45, -2.3) * mm, "end": v(24.47, -2.41) * mm});
            skLineSegment(sketch, "E51.10.3", {"start": v(27.44, -1.7) * mm, "end": v(28.03, -1.43) * mm});
            skLineSegment(sketch, "E51.10.4", {"start": v(27.48, -1) * mm, "end": v(28.03, -1.32) * mm});
            skLineSegment(sketch, "E51.10.5", {"start": v(28.03, -1.32) * mm, "end": v(28.63, -1.7) * mm});
            skLineSegment(sketch, "E51.10.6", {"start": v(26.9, -1.91) * mm, "end": v(27.44, -1.7) * mm});
            skLineSegment(sketch, "E51.10.7", {"start": v(29.32, -0.72) * mm, "end": v(30.02, -0.27) * mm});
            skLineSegment(sketch, "E51.10.8", {"start": v(26.4, -2.08) * mm, "end": v(26.9, -1.91) * mm});
            skLineSegment(sketch, "E51.10.9", {"start": v(29.25, -2.16) * mm, "end": v(29.9, -2.68) * mm});
            skLineSegment(sketch, "E51.10.10", {"start": v(28.66, -1.1) * mm, "end": v(29.32, -0.72) * mm});
            skLineSegment(sketch, "E51.10.11", {"start": v(26.96, -0.73) * mm, "end": v(27.48, -1) * mm});
            skLineSegment(sketch, "E51.10.12", {"start": v(28.63, -1.7) * mm, "end": v(29.25, -2.16) * mm});
            skLineSegment(sketch, "E51.10.13", {"start": v(25.24, -2.36) * mm, "end": v(25.57, -2.3) * mm});
            skLineSegment(sketch, "E51.10.14", {"start": v(25.57, -2.3) * mm, "end": v(25.96, -2.2) * mm});
            skLineSegment(sketch, "E51.10.15", {"start": v(25.96, -2.2) * mm, "end": v(26.4, -2.08) * mm});
            skLineSegment(sketch, "E51.10.16", {"start": v(26.05, -0.35) * mm, "end": v(26.48, -0.52) * mm});
            skLineSegment(sketch, "E51.10.17", {"start": v(25.67, -0.22) * mm, "end": v(26.05, -0.35) * mm});
            skLineSegment(sketch, "E51.10.18", {"start": v(26.48, -0.52) * mm, "end": v(26.96, -0.73) * mm});
            skLineSegment(sketch, "E51.10.19", {"start": v(24.96, -2.4) * mm, "end": v(25.24, -2.36) * mm});
            skLineSegment(sketch, "E51.10.20", {"start": v(24.75, -2.4) * mm, "end": v(24.96, -2.4) * mm});
            skLineSegment(sketch, "E51.10.21", {"start": v(25.35, -0.13) * mm, "end": v(25.67, -0.22) * mm});
            skLineSegment(sketch, "E51.10.22", {"start": v(25.08, -0.07) * mm, "end": v(25.35, -0.13) * mm});
            skLineSegment(sketch, "E51.10.23", {"start": v(24.71, 0) * mm, "end": v(24.87, -0.03) * mm});
            skLineSegment(sketch, "E51.10.24", {"start": v(24.47, -2.41) * mm, "end": v(24.5, -2.41) * mm});
            skLineSegment(sketch, "E51.10.25", {"start": v(24.5, -2.41) * mm, "end": v(24.6, -2.41) * mm});
            skLineSegment(sketch, "E51.10.26", {"start": v(24.87, -0.03) * mm, "end": v(25.08, -0.07) * mm});
            skLineSegment(sketch, "E51.10.27", {"start": v(24.6, -2.41) * mm, "end": v(24.75, -2.4) * mm});
            skLineSegment(sketch, "E51.10.28", {"start": v(24.62, 0) * mm, "end": v(24.71, 0) * mm});
            skLineSegment(sketch, "E51.10.29", {"start": v(24.6, 0) * mm, "end": v(24.62, 0) * mm});
            skLineSegment(sketch, "E51.11.0", {"start": v(22.4, 7.28) * mm, "end": v(23.39, 7.6) * mm});
            skLineSegment(sketch, "E51.11.1", {"start": v(27.1, 7.3) * mm, "end": v(27.6, 7.8) * mm});
            skLineSegment(sketch, "E51.11.2", {"start": v(23.02, 5.05) * mm, "end": v(24.02, 5.27) * mm});
            skLineSegment(sketch, "E51.11.3", {"start": v(26.62, 6.86) * mm, "end": v(27.1, 7.3) * mm});
            skLineSegment(sketch, "E51.11.4", {"start": v(26.44, 7.54) * mm, "end": v(27.07, 7.4) * mm});
            skLineSegment(sketch, "E51.11.5", {"start": v(27.07, 7.4) * mm, "end": v(27.75, 7.22) * mm});
            skLineSegment(sketch, "E51.11.6", {"start": v(26.17, 6.5) * mm, "end": v(26.62, 6.86) * mm});
            skLineSegment(sketch, "E51.11.7", {"start": v(28.1, 8.38) * mm, "end": v(28.63, 9.02) * mm});
            skLineSegment(sketch, "E51.11.8", {"start": v(25.75, 6.18) * mm, "end": v(26.17, 6.5) * mm});
            skLineSegment(sketch, "E51.11.9", {"start": v(28.48, 6.99) * mm, "end": v(29.26, 6.7) * mm});
            skLineSegment(sketch, "E51.11.10", {"start": v(27.6, 7.8) * mm, "end": v(28.1, 8.38) * mm});
            skLineSegment(sketch, "E51.11.11", {"start": v(25.86, 7.63) * mm, "end": v(26.44, 7.54) * mm});
            skLineSegment(sketch, "E51.11.12", {"start": v(27.75, 7.22) * mm, "end": v(28.48, 6.99) * mm});
            skLineSegment(sketch, "E51.11.13", {"start": v(24.73, 5.56) * mm, "end": v(25.03, 5.72) * mm});
            skLineSegment(sketch, "E51.11.14", {"start": v(25.03, 5.72) * mm, "end": v(25.37, 5.92) * mm});
            skLineSegment(sketch, "E51.11.15", {"start": v(25.37, 5.92) * mm, "end": v(25.75, 6.18) * mm});
            skLineSegment(sketch, "E51.11.16", {"start": v(24.88, 7.72) * mm, "end": v(25.34, 7.7) * mm});
            skLineSegment(sketch, "E51.11.17", {"start": v(24.48, 7.72) * mm, "end": v(24.88, 7.72) * mm});
            skLineSegment(sketch, "E51.11.18", {"start": v(25.34, 7.7) * mm, "end": v(25.86, 7.63) * mm});
            skLineSegment(sketch, "E51.11.19", {"start": v(24.48, 5.44) * mm, "end": v(24.73, 5.56) * mm});
            skLineSegment(sketch, "E51.11.20", {"start": v(24.28, 5.36) * mm, "end": v(24.48, 5.44) * mm});
            skLineSegment(sketch, "E51.11.21", {"start": v(24.15, 7.71) * mm, "end": v(24.48, 7.72) * mm});
            skLineSegment(sketch, "E51.11.22", {"start": v(23.87, 7.69) * mm, "end": v(24.15, 7.71) * mm});
            skLineSegment(sketch, "E51.11.23", {"start": v(23.5, 7.63) * mm, "end": v(23.66, 7.66) * mm});
            skLineSegment(sketch, "E51.11.24", {"start": v(24.02, 5.27) * mm, "end": v(24.05, 5.28) * mm});
            skLineSegment(sketch, "E51.11.25", {"start": v(24.05, 5.28) * mm, "end": v(24.14, 5.3) * mm});
            skLineSegment(sketch, "E51.11.26", {"start": v(23.66, 7.66) * mm, "end": v(23.87, 7.69) * mm});
            skLineSegment(sketch, "E51.11.27", {"start": v(24.14, 5.3) * mm, "end": v(24.28, 5.36) * mm});
            skLineSegment(sketch, "E51.11.28", {"start": v(23.42, 7.6) * mm, "end": v(23.5, 7.63) * mm});
            skLineSegment(sketch, "E51.11.29", {"start": v(23.39, 7.6) * mm, "end": v(23.42, 7.6) * mm});
            skLineSegment(sketch, "E51.12.0", {"start": v(19.06, 13.85) * mm, "end": v(19.9, 14.45) * mm});
            skLineSegment(sketch, "E51.12.1", {"start": v(23.52, 15.32) * mm, "end": v(23.83, 15.95) * mm});
            skLineSegment(sketch, "E51.12.2", {"start": v(20.33, 11.91) * mm, "end": v(21.22, 12.43) * mm});
            skLineSegment(sketch, "E51.12.3", {"start": v(23.2, 14.76) * mm, "end": v(23.52, 15.32) * mm});
            skLineSegment(sketch, "E51.12.4", {"start": v(22.82, 15.34) * mm, "end": v(23.46, 15.4) * mm});
            skLineSegment(sketch, "E51.12.5", {"start": v(23.46, 15.4) * mm, "end": v(24.16, 15.44) * mm});
            skLineSegment(sketch, "E51.12.6", {"start": v(22.89, 14.26) * mm, "end": v(23.2, 14.76) * mm});
            skLineSegment(sketch, "E51.12.7", {"start": v(24.14, 16.65) * mm, "end": v(24.44, 17.43) * mm});
            skLineSegment(sketch, "E51.12.8", {"start": v(22.58, 13.84) * mm, "end": v(22.89, 14.26) * mm});
            skLineSegment(sketch, "E51.12.9", {"start": v(24.93, 15.45) * mm, "end": v(25.76, 15.4) * mm});
            skLineSegment(sketch, "E51.12.10", {"start": v(23.83, 15.95) * mm, "end": v(24.14, 16.65) * mm});
            skLineSegment(sketch, "E51.12.11", {"start": v(22.24, 15.25) * mm, "end": v(22.82, 15.34) * mm});
            skLineSegment(sketch, "E51.12.12", {"start": v(24.16, 15.44) * mm, "end": v(24.93, 15.45) * mm});
            skLineSegment(sketch, "E51.12.13", {"start": v(21.8, 12.93) * mm, "end": v(22.04, 13.17) * mm});
            skLineSegment(sketch, "E51.12.14", {"start": v(22.04, 13.17) * mm, "end": v(22.3, 13.47) * mm});
            skLineSegment(sketch, "E51.12.15", {"start": v(22.3, 13.47) * mm, "end": v(22.58, 13.84) * mm});
            skLineSegment(sketch, "E51.12.16", {"start": v(21.28, 15.03) * mm, "end": v(21.73, 15.15) * mm});
            skLineSegment(sketch, "E51.12.17", {"start": v(20.9, 14.91) * mm, "end": v(21.28, 15.03) * mm});
            skLineSegment(sketch, "E51.12.18", {"start": v(21.73, 15.15) * mm, "end": v(22.24, 15.25) * mm});
            skLineSegment(sketch, "E51.12.19", {"start": v(21.6, 12.74) * mm, "end": v(21.8, 12.93) * mm});
            skLineSegment(sketch, "E51.12.20", {"start": v(21.44, 12.6) * mm, "end": v(21.6, 12.74) * mm});
            skLineSegment(sketch, "E51.12.21", {"start": v(20.58, 14.8) * mm, "end": v(20.9, 14.91) * mm});
            skLineSegment(sketch, "E51.12.22", {"start": v(20.33, 14.69) * mm, "end": v(20.58, 14.8) * mm});
            skLineSegment(sketch, "E51.12.23", {"start": v(20, 14.52) * mm, "end": v(20.13, 14.6) * mm});
            skLineSegment(sketch, "E51.12.24", {"start": v(21.22, 12.43) * mm, "end": v(21.24, 12.45) * mm});
            skLineSegment(sketch, "E51.12.25", {"start": v(21.24, 12.45) * mm, "end": v(21.32, 12.5) * mm});
            skLineSegment(sketch, "E51.12.26", {"start": v(20.13, 14.6) * mm, "end": v(20.33, 14.69) * mm});
            skLineSegment(sketch, "E51.12.27", {"start": v(21.32, 12.5) * mm, "end": v(21.44, 12.6) * mm});
            skLineSegment(sketch, "E51.12.28", {"start": v(19.92, 14.47) * mm, "end": v(20, 14.52) * mm});
            skLineSegment(sketch, "E51.12.29", {"start": v(19.9, 14.45) * mm, "end": v(19.92, 14.47) * mm});
            skLineSegment(sketch, "E51.13.0", {"start": v(13.85, 19.06) * mm, "end": v(14.45, 19.9) * mm});
            skLineSegment(sketch, "E51.13.1", {"start": v(17.63, 21.83) * mm, "end": v(17.74, 22.53) * mm});
            skLineSegment(sketch, "E51.13.2", {"start": v(15.65, 17.61) * mm, "end": v(16.33, 18.38) * mm});
            skLineSegment(sketch, "E51.13.3", {"start": v(17.5, 21.2) * mm, "end": v(17.63, 21.83) * mm});
            skLineSegment(sketch, "E51.13.4", {"start": v(16.96, 21.64) * mm, "end": v(17.55, 21.9) * mm});
            skLineSegment(sketch, "E51.13.5", {"start": v(17.55, 21.9) * mm, "end": v(18.2, 22.16) * mm});
            skLineSegment(sketch, "E51.13.6", {"start": v(17.36, 20.64) * mm, "end": v(17.5, 21.2) * mm});
            skLineSegment(sketch, "E51.13.7", {"start": v(17.82, 23.3) * mm, "end": v(17.86, 24.13) * mm});
            skLineSegment(sketch, "E51.13.8", {"start": v(17.2, 20.14) * mm, "end": v(17.36, 20.64) * mm});
            skLineSegment(sketch, "E51.13.9", {"start": v(18.94, 22.4) * mm, "end": v(19.74, 22.61) * mm});
            skLineSegment(sketch, "E51.13.10", {"start": v(17.74, 22.53) * mm, "end": v(17.82, 23.3) * mm});
            skLineSegment(sketch, "E51.13.11", {"start": v(16.44, 21.38) * mm, "end": v(16.96, 21.64) * mm});
            skLineSegment(sketch, "E51.13.12", {"start": v(18.2, 22.16) * mm, "end": v(18.94, 22.4) * mm});
            skLineSegment(sketch, "E51.13.13", {"start": v(16.74, 19.03) * mm, "end": v(16.89, 19.34) * mm});
            skLineSegment(sketch, "E51.13.14", {"start": v(16.89, 19.34) * mm, "end": v(17.05, 19.7) * mm});
            skLineSegment(sketch, "E51.13.15", {"start": v(17.05, 19.7) * mm, "end": v(17.2, 20.14) * mm});
            skLineSegment(sketch, "E51.13.16", {"start": v(15.6, 20.87) * mm, "end": v(15.98, 21.12) * mm});
            skLineSegment(sketch, "E51.13.17", {"start": v(15.27, 20.64) * mm, "end": v(15.6, 20.87) * mm});
            skLineSegment(sketch, "E51.13.18", {"start": v(15.98, 21.12) * mm, "end": v(16.44, 21.38) * mm});
            skLineSegment(sketch, "E51.13.19", {"start": v(16.6, 18.79) * mm, "end": v(16.74, 19.03) * mm});
            skLineSegment(sketch, "E51.13.20", {"start": v(16.5, 18.6) * mm, "end": v(16.6, 18.79) * mm});
            skLineSegment(sketch, "E51.13.21", {"start": v(15, 20.43) * mm, "end": v(15.27, 20.64) * mm});
            skLineSegment(sketch, "E51.13.22", {"start": v(14.8, 20.25) * mm, "end": v(15, 20.43) * mm});
            skLineSegment(sketch, "E51.13.23", {"start": v(14.53, 19.99) * mm, "end": v(14.64, 20.1) * mm});
            skLineSegment(sketch, "E51.13.24", {"start": v(16.33, 18.38) * mm, "end": v(16.35, 18.4) * mm});
            skLineSegment(sketch, "E51.13.25", {"start": v(16.35, 18.4) * mm, "end": v(16.4, 18.48) * mm});
            skLineSegment(sketch, "E51.13.26", {"start": v(14.64, 20.1) * mm, "end": v(14.8, 20.25) * mm});
            skLineSegment(sketch, "E51.13.27", {"start": v(16.4, 18.48) * mm, "end": v(16.5, 18.6) * mm});
            skLineSegment(sketch, "E51.13.28", {"start": v(14.47, 19.92) * mm, "end": v(14.53, 19.99) * mm});
            skLineSegment(sketch, "E51.13.29", {"start": v(14.45, 19.9) * mm, "end": v(14.47, 19.92) * mm});
            skLineSegment(sketch, "E51.14.0", {"start": v(7.28, 22.4) * mm, "end": v(7.6, 23.39) * mm});
            skLineSegment(sketch, "E51.14.1", {"start": v(10.02, 26.21) * mm, "end": v(9.9, 26.91) * mm});
            skLineSegment(sketch, "E51.14.2", {"start": v(9.44, 21.59) * mm, "end": v(9.85, 22.53) * mm});
            skLineSegment(sketch, "E51.14.3", {"start": v(10.1, 25.57) * mm, "end": v(10.02, 26.21) * mm});
            skLineSegment(sketch, "E51.14.4", {"start": v(9.44, 25.82) * mm, "end": v(9.92, 26.25) * mm});
            skLineSegment(sketch, "E51.14.5", {"start": v(9.92, 26.25) * mm, "end": v(10.47, 26.7) * mm});
            skLineSegment(sketch, "E51.14.6", {"start": v(10.13, 25) * mm, "end": v(10.1, 25.57) * mm});
            skLineSegment(sketch, "E51.14.7", {"start": v(9.75, 27.66) * mm, "end": v(9.53, 28.46) * mm});
            skLineSegment(sketch, "E51.14.8", {"start": v(10.14, 24.47) * mm, "end": v(10.13, 25) * mm});
            skLineSegment(sketch, "E51.14.9", {"start": v(11.1, 27.15) * mm, "end": v(11.78, 27.6) * mm});
            skLineSegment(sketch, "E51.14.10", {"start": v(9.9, 26.91) * mm, "end": v(9.75, 27.66) * mm});
            skLineSegment(sketch, "E51.14.11", {"start": v(9.03, 25.41) * mm, "end": v(9.44, 25.82) * mm});
            skLineSegment(sketch, "E51.14.12", {"start": v(10.47, 26.7) * mm, "end": v(11.1, 27.15) * mm});
            skLineSegment(sketch, "E51.14.13", {"start": v(10.04, 23.27) * mm, "end": v(10.09, 23.6) * mm});
            skLineSegment(sketch, "E51.14.14", {"start": v(10.09, 23.6) * mm, "end": v(10.12, 24) * mm});
            skLineSegment(sketch, "E51.14.15", {"start": v(10.12, 24) * mm, "end": v(10.14, 24.47) * mm});
            skLineSegment(sketch, "E51.14.16", {"start": v(8.38, 24.67) * mm, "end": v(8.67, 25.02) * mm});
            skLineSegment(sketch, "E51.14.17", {"start": v(8.14, 24.35) * mm, "end": v(8.38, 24.67) * mm});
            skLineSegment(sketch, "E51.14.18", {"start": v(8.67, 25.02) * mm, "end": v(9.03, 25.41) * mm});
            skLineSegment(sketch, "E51.14.19", {"start": v(10, 23) * mm, "end": v(10.04, 23.27) * mm});
            skLineSegment(sketch, "E51.14.20", {"start": v(9.94, 22.8) * mm, "end": v(10, 23) * mm});
            skLineSegment(sketch, "E51.14.21", {"start": v(7.95, 24.07) * mm, "end": v(8.14, 24.35) * mm});
            skLineSegment(sketch, "E51.14.22", {"start": v(7.81, 23.83) * mm, "end": v(7.95, 24.07) * mm});
            skLineSegment(sketch, "E51.14.23", {"start": v(7.64, 23.5) * mm, "end": v(7.71, 23.64) * mm});
            skLineSegment(sketch, "E51.14.24", {"start": v(9.85, 22.53) * mm, "end": v(9.87, 22.56) * mm});
            skLineSegment(sketch, "E51.14.25", {"start": v(9.87, 22.56) * mm, "end": v(9.9, 22.65) * mm});
            skLineSegment(sketch, "E51.14.26", {"start": v(7.71, 23.64) * mm, "end": v(7.81, 23.83) * mm});
            skLineSegment(sketch, "E51.14.27", {"start": v(9.9, 22.65) * mm, "end": v(9.94, 22.8) * mm});
            skLineSegment(sketch, "E51.14.28", {"start": v(7.6, 23.42) * mm, "end": v(7.64, 23.5) * mm});
            skLineSegment(sketch, "E51.14.29", {"start": v(7.6, 23.39) * mm, "end": v(7.6, 23.42) * mm});
            skLineSegment(sketch, "E51.15.0", {"start": v(0, 23.56) * mm, "end": v(0, 24.6) * mm});
            skLineSegment(sketch, "E51.15.1", {"start": v(1.43, 28.03) * mm, "end": v(1.1, 28.66) * mm});
            skLineSegment(sketch, "E51.15.2", {"start": v(2.3, 23.45) * mm, "end": v(2.41, 24.47) * mm});
            skLineSegment(sketch, "E51.15.3", {"start": v(1.7, 27.44) * mm, "end": v(1.43, 28.03) * mm});
            skLineSegment(sketch, "E51.15.4", {"start": v(1, 27.48) * mm, "end": v(1.32, 28.03) * mm});
            skLineSegment(sketch, "E51.15.5", {"start": v(1.32, 28.03) * mm, "end": v(1.7, 28.63) * mm});
            skLineSegment(sketch, "E51.15.6", {"start": v(1.91, 26.9) * mm, "end": v(1.7, 27.44) * mm});
            skLineSegment(sketch, "E51.15.7", {"start": v(0.72, 29.32) * mm, "end": v(0.27, 30.02) * mm});
            skLineSegment(sketch, "E51.15.8", {"start": v(2.08, 26.4) * mm, "end": v(1.91, 26.9) * mm});
            skLineSegment(sketch, "E51.15.9", {"start": v(2.16, 29.25) * mm, "end": v(2.68, 29.9) * mm});
            skLineSegment(sketch, "E51.15.10", {"start": v(1.1, 28.66) * mm, "end": v(0.72, 29.32) * mm});
            skLineSegment(sketch, "E51.15.11", {"start": v(0.73, 26.96) * mm, "end": v(1, 27.48) * mm});
            skLineSegment(sketch, "E51.15.12", {"start": v(1.7, 28.63) * mm, "end": v(2.16, 29.25) * mm});
            skLineSegment(sketch, "E51.15.13", {"start": v(2.36, 25.24) * mm, "end": v(2.3, 25.57) * mm});
            skLineSegment(sketch, "E51.15.14", {"start": v(2.3, 25.57) * mm, "end": v(2.2, 25.96) * mm});
            skLineSegment(sketch, "E51.15.15", {"start": v(2.2, 25.96) * mm, "end": v(2.08, 26.4) * mm});
            skLineSegment(sketch, "E51.15.16", {"start": v(0.35, 26.05) * mm, "end": v(0.52, 26.48) * mm});
            skLineSegment(sketch, "E51.15.17", {"start": v(0.22, 25.67) * mm, "end": v(0.35, 26.05) * mm});
            skLineSegment(sketch, "E51.15.18", {"start": v(0.52, 26.48) * mm, "end": v(0.73, 26.96) * mm});
            skLineSegment(sketch, "E51.15.19", {"start": v(2.4, 24.96) * mm, "end": v(2.36, 25.24) * mm});
            skLineSegment(sketch, "E51.15.20", {"start": v(2.4, 24.75) * mm, "end": v(2.4, 24.96) * mm});
            skLineSegment(sketch, "E51.15.21", {"start": v(0.13, 25.35) * mm, "end": v(0.22, 25.67) * mm});
            skLineSegment(sketch, "E51.15.22", {"start": v(0.07, 25.08) * mm, "end": v(0.13, 25.35) * mm});
            skLineSegment(sketch, "E51.15.23", {"start": v(0, 24.71) * mm, "end": v(0.03, 24.87) * mm});
            skLineSegment(sketch, "E51.15.24", {"start": v(2.41, 24.47) * mm, "end": v(2.41, 24.5) * mm});
            skLineSegment(sketch, "E51.15.25", {"start": v(2.41, 24.5) * mm, "end": v(2.41, 24.6) * mm});
            skLineSegment(sketch, "E51.15.26", {"start": v(0.03, 24.87) * mm, "end": v(0.07, 25.08) * mm});
            skLineSegment(sketch, "E51.15.27", {"start": v(2.41, 24.6) * mm, "end": v(2.4, 24.75) * mm});
            skLineSegment(sketch, "E51.15.28", {"start": v(0, 24.62) * mm, "end": v(0, 24.71) * mm});
            skLineSegment(sketch, "E51.15.29", {"start": v(0, 24.6) * mm, "end": v(0, 24.62) * mm});
            skLineSegment(sketch, "E51.16.0", {"start": v(-7.28, 22.4) * mm, "end": v(-7.6, 23.39) * mm});
            skLineSegment(sketch, "E51.16.1", {"start": v(-7.3, 27.1) * mm, "end": v(-7.8, 27.6) * mm});
            skLineSegment(sketch, "E51.16.2", {"start": v(-5.05, 23.02) * mm, "end": v(-5.27, 24.02) * mm});
            skLineSegment(sketch, "E51.16.3", {"start": v(-6.86, 26.62) * mm, "end": v(-7.3, 27.1) * mm});
            skLineSegment(sketch, "E51.16.4", {"start": v(-7.54, 26.44) * mm, "end": v(-7.4, 27.07) * mm});
            skLineSegment(sketch, "E51.16.5", {"start": v(-7.4, 27.07) * mm, "end": v(-7.22, 27.75) * mm});
            skLineSegment(sketch, "E51.16.6", {"start": v(-6.5, 26.17) * mm, "end": v(-6.86, 26.62) * mm});
            skLineSegment(sketch, "E51.16.7", {"start": v(-8.38, 28.1) * mm, "end": v(-9.02, 28.63) * mm});
            skLineSegment(sketch, "E51.16.8", {"start": v(-6.18, 25.75) * mm, "end": v(-6.5, 26.17) * mm});
            skLineSegment(sketch, "E51.16.9", {"start": v(-6.99, 28.48) * mm, "end": v(-6.7, 29.26) * mm});
            skLineSegment(sketch, "E51.16.10", {"start": v(-7.8, 27.6) * mm, "end": v(-8.38, 28.1) * mm});
            skLineSegment(sketch, "E51.16.11", {"start": v(-7.63, 25.86) * mm, "end": v(-7.54, 26.44) * mm});
            skLineSegment(sketch, "E51.16.12", {"start": v(-7.22, 27.75) * mm, "end": v(-6.99, 28.48) * mm});
            skLineSegment(sketch, "E51.16.13", {"start": v(-5.56, 24.73) * mm, "end": v(-5.72, 25.03) * mm});
            skLineSegment(sketch, "E51.16.14", {"start": v(-5.72, 25.03) * mm, "end": v(-5.92, 25.37) * mm});
            skLineSegment(sketch, "E51.16.15", {"start": v(-5.92, 25.37) * mm, "end": v(-6.18, 25.75) * mm});
            skLineSegment(sketch, "E51.16.16", {"start": v(-7.72, 24.88) * mm, "end": v(-7.7, 25.34) * mm});
            skLineSegment(sketch, "E51.16.17", {"start": v(-7.72, 24.48) * mm, "end": v(-7.72, 24.88) * mm});
            skLineSegment(sketch, "E51.16.18", {"start": v(-7.7, 25.34) * mm, "end": v(-7.63, 25.86) * mm});
            skLineSegment(sketch, "E51.16.19", {"start": v(-5.44, 24.48) * mm, "end": v(-5.56, 24.73) * mm});
            skLineSegment(sketch, "E51.16.20", {"start": v(-5.36, 24.28) * mm, "end": v(-5.44, 24.48) * mm});
            skLineSegment(sketch, "E51.16.21", {"start": v(-7.71, 24.15) * mm, "end": v(-7.72, 24.48) * mm});
            skLineSegment(sketch, "E51.16.22", {"start": v(-7.69, 23.87) * mm, "end": v(-7.71, 24.15) * mm});
            skLineSegment(sketch, "E51.16.23", {"start": v(-7.63, 23.5) * mm, "end": v(-7.66, 23.66) * mm});
            skLineSegment(sketch, "E51.16.24", {"start": v(-5.27, 24.02) * mm, "end": v(-5.28, 24.05) * mm});
            skLineSegment(sketch, "E51.16.25", {"start": v(-5.28, 24.05) * mm, "end": v(-5.3, 24.14) * mm});
            skLineSegment(sketch, "E51.16.26", {"start": v(-7.66, 23.66) * mm, "end": v(-7.69, 23.87) * mm});
            skLineSegment(sketch, "E51.16.27", {"start": v(-5.3, 24.14) * mm, "end": v(-5.36, 24.28) * mm});
            skLineSegment(sketch, "E51.16.28", {"start": v(-7.6, 23.42) * mm, "end": v(-7.63, 23.5) * mm});
            skLineSegment(sketch, "E51.16.29", {"start": v(-7.6, 23.39) * mm, "end": v(-7.6, 23.42) * mm});
            skLineSegment(sketch, "E51.17.0", {"start": v(-13.85, 19.06) * mm, "end": v(-14.45, 19.9) * mm});
            skLineSegment(sketch, "E51.17.1", {"start": v(-15.32, 23.52) * mm, "end": v(-15.95, 23.83) * mm});
            skLineSegment(sketch, "E51.17.2", {"start": v(-11.91, 20.33) * mm, "end": v(-12.43, 21.22) * mm});
            skLineSegment(sketch, "E51.17.3", {"start": v(-14.76, 23.2) * mm, "end": v(-15.32, 23.52) * mm});
            skLineSegment(sketch, "E51.17.4", {"start": v(-15.34, 22.82) * mm, "end": v(-15.4, 23.46) * mm});
            skLineSegment(sketch, "E51.17.5", {"start": v(-15.4, 23.46) * mm, "end": v(-15.44, 24.16) * mm});
            skLineSegment(sketch, "E51.17.6", {"start": v(-14.26, 22.89) * mm, "end": v(-14.76, 23.2) * mm});
            skLineSegment(sketch, "E51.17.7", {"start": v(-16.65, 24.14) * mm, "end": v(-17.43, 24.44) * mm});
            skLineSegment(sketch, "E51.17.8", {"start": v(-13.84, 22.58) * mm, "end": v(-14.26, 22.89) * mm});
            skLineSegment(sketch, "E51.17.9", {"start": v(-15.45, 24.93) * mm, "end": v(-15.4, 25.76) * mm});
            skLineSegment(sketch, "E51.17.10", {"start": v(-15.95, 23.83) * mm, "end": v(-16.65, 24.14) * mm});
            skLineSegment(sketch, "E51.17.11", {"start": v(-15.25, 22.24) * mm, "end": v(-15.34, 22.82) * mm});
            skLineSegment(sketch, "E51.17.12", {"start": v(-15.44, 24.16) * mm, "end": v(-15.45, 24.93) * mm});
            skLineSegment(sketch, "E51.17.13", {"start": v(-12.93, 21.8) * mm, "end": v(-13.17, 22.04) * mm});
            skLineSegment(sketch, "E51.17.14", {"start": v(-13.17, 22.04) * mm, "end": v(-13.47, 22.3) * mm});
            skLineSegment(sketch, "E51.17.15", {"start": v(-13.47, 22.3) * mm, "end": v(-13.84, 22.58) * mm});
            skLineSegment(sketch, "E51.17.16", {"start": v(-15.03, 21.28) * mm, "end": v(-15.15, 21.73) * mm});
            skLineSegment(sketch, "E51.17.17", {"start": v(-14.91, 20.9) * mm, "end": v(-15.03, 21.28) * mm});
            skLineSegment(sketch, "E51.17.18", {"start": v(-15.15, 21.73) * mm, "end": v(-15.25, 22.24) * mm});
            skLineSegment(sketch, "E51.17.19", {"start": v(-12.74, 21.6) * mm, "end": v(-12.93, 21.8) * mm});
            skLineSegment(sketch, "E51.17.20", {"start": v(-12.6, 21.44) * mm, "end": v(-12.74, 21.6) * mm});
            skLineSegment(sketch, "E51.17.21", {"start": v(-14.8, 20.58) * mm, "end": v(-14.91, 20.9) * mm});
            skLineSegment(sketch, "E51.17.22", {"start": v(-14.69, 20.33) * mm, "end": v(-14.8, 20.58) * mm});
            skLineSegment(sketch, "E51.17.23", {"start": v(-14.52, 20) * mm, "end": v(-14.6, 20.13) * mm});
            skLineSegment(sketch, "E51.17.24", {"start": v(-12.43, 21.22) * mm, "end": v(-12.45, 21.24) * mm});
            skLineSegment(sketch, "E51.17.25", {"start": v(-12.45, 21.24) * mm, "end": v(-12.5, 21.32) * mm});
            skLineSegment(sketch, "E51.17.26", {"start": v(-14.6, 20.13) * mm, "end": v(-14.69, 20.33) * mm});
            skLineSegment(sketch, "E51.17.27", {"start": v(-12.5, 21.32) * mm, "end": v(-12.6, 21.44) * mm});
            skLineSegment(sketch, "E51.17.28", {"start": v(-14.47, 19.92) * mm, "end": v(-14.52, 20) * mm});
            skLineSegment(sketch, "E51.17.29", {"start": v(-14.45, 19.9) * mm, "end": v(-14.47, 19.92) * mm});
            skLineSegment(sketch, "E51.18.0", {"start": v(-19.06, 13.85) * mm, "end": v(-19.9, 14.45) * mm});
            skLineSegment(sketch, "E51.18.1", {"start": v(-21.83, 17.63) * mm, "end": v(-22.53, 17.74) * mm});
            skLineSegment(sketch, "E51.18.2", {"start": v(-17.61, 15.65) * mm, "end": v(-18.38, 16.33) * mm});
            skLineSegment(sketch, "E51.18.3", {"start": v(-21.2, 17.5) * mm, "end": v(-21.83, 17.63) * mm});
            skLineSegment(sketch, "E51.18.4", {"start": v(-21.64, 16.96) * mm, "end": v(-21.9, 17.55) * mm});
            skLineSegment(sketch, "E51.18.5", {"start": v(-21.9, 17.55) * mm, "end": v(-22.16, 18.2) * mm});
            skLineSegment(sketch, "E51.18.6", {"start": v(-20.64, 17.36) * mm, "end": v(-21.2, 17.5) * mm});
            skLineSegment(sketch, "E51.18.7", {"start": v(-23.3, 17.82) * mm, "end": v(-24.13, 17.86) * mm});
            skLineSegment(sketch, "E51.18.8", {"start": v(-20.14, 17.2) * mm, "end": v(-20.64, 17.36) * mm});
            skLineSegment(sketch, "E51.18.9", {"start": v(-22.4, 18.94) * mm, "end": v(-22.61, 19.74) * mm});
            skLineSegment(sketch, "E51.18.10", {"start": v(-22.53, 17.74) * mm, "end": v(-23.3, 17.82) * mm});
            skLineSegment(sketch, "E51.18.11", {"start": v(-21.38, 16.44) * mm, "end": v(-21.64, 16.96) * mm});
            skLineSegment(sketch, "E51.18.12", {"start": v(-22.16, 18.2) * mm, "end": v(-22.4, 18.94) * mm});
            skLineSegment(sketch, "E51.18.13", {"start": v(-19.03, 16.74) * mm, "end": v(-19.34, 16.89) * mm});
            skLineSegment(sketch, "E51.18.14", {"start": v(-19.34, 16.89) * mm, "end": v(-19.7, 17.05) * mm});
            skLineSegment(sketch, "E51.18.15", {"start": v(-19.7, 17.05) * mm, "end": v(-20.14, 17.2) * mm});
            skLineSegment(sketch, "E51.18.16", {"start": v(-20.87, 15.6) * mm, "end": v(-21.12, 15.98) * mm});
            skLineSegment(sketch, "E51.18.17", {"start": v(-20.64, 15.27) * mm, "end": v(-20.87, 15.6) * mm});
            skLineSegment(sketch, "E51.18.18", {"start": v(-21.12, 15.98) * mm, "end": v(-21.38, 16.44) * mm});
            skLineSegment(sketch, "E51.18.19", {"start": v(-18.79, 16.6) * mm, "end": v(-19.03, 16.74) * mm});
            skLineSegment(sketch, "E51.18.20", {"start": v(-18.6, 16.5) * mm, "end": v(-18.79, 16.6) * mm});
            skLineSegment(sketch, "E51.18.21", {"start": v(-20.43, 15) * mm, "end": v(-20.64, 15.27) * mm});
            skLineSegment(sketch, "E51.18.22", {"start": v(-20.25, 14.8) * mm, "end": v(-20.43, 15) * mm});
            skLineSegment(sketch, "E51.18.23", {"start": v(-19.99, 14.53) * mm, "end": v(-20.1, 14.64) * mm});
            skLineSegment(sketch, "E51.18.24", {"start": v(-18.38, 16.33) * mm, "end": v(-18.4, 16.35) * mm});
            skLineSegment(sketch, "E51.18.25", {"start": v(-18.4, 16.35) * mm, "end": v(-18.48, 16.4) * mm});
            skLineSegment(sketch, "E51.18.26", {"start": v(-20.1, 14.64) * mm, "end": v(-20.25, 14.8) * mm});
            skLineSegment(sketch, "E51.18.27", {"start": v(-18.48, 16.4) * mm, "end": v(-18.6, 16.5) * mm});
            skLineSegment(sketch, "E51.18.28", {"start": v(-19.92, 14.47) * mm, "end": v(-19.99, 14.53) * mm});
            skLineSegment(sketch, "E51.18.29", {"start": v(-19.9, 14.45) * mm, "end": v(-19.92, 14.47) * mm});
            skLineSegment(sketch, "E51.19.0", {"start": v(-22.4, 7.28) * mm, "end": v(-23.39, 7.6) * mm});
            skLineSegment(sketch, "E51.19.1", {"start": v(-26.21, 10.02) * mm, "end": v(-26.91, 9.9) * mm});
            skLineSegment(sketch, "E51.19.2", {"start": v(-21.59, 9.44) * mm, "end": v(-22.53, 9.85) * mm});
            skLineSegment(sketch, "E51.19.3", {"start": v(-25.57, 10.1) * mm, "end": v(-26.21, 10.02) * mm});
            skLineSegment(sketch, "E51.19.4", {"start": v(-25.82, 9.44) * mm, "end": v(-26.25, 9.92) * mm});
            skLineSegment(sketch, "E51.19.5", {"start": v(-26.25, 9.92) * mm, "end": v(-26.7, 10.47) * mm});
            skLineSegment(sketch, "E51.19.6", {"start": v(-25, 10.13) * mm, "end": v(-25.57, 10.1) * mm});
            skLineSegment(sketch, "E51.19.7", {"start": v(-27.66, 9.75) * mm, "end": v(-28.46, 9.53) * mm});
            skLineSegment(sketch, "E51.19.8", {"start": v(-24.47, 10.14) * mm, "end": v(-25, 10.13) * mm});
            skLineSegment(sketch, "E51.19.9", {"start": v(-27.15, 11.1) * mm, "end": v(-27.6, 11.78) * mm});
            skLineSegment(sketch, "E51.19.10", {"start": v(-26.91, 9.9) * mm, "end": v(-27.66, 9.75) * mm});
            skLineSegment(sketch, "E51.19.11", {"start": v(-25.41, 9.03) * mm, "end": v(-25.82, 9.44) * mm});
            skLineSegment(sketch, "E51.19.12", {"start": v(-26.7, 10.47) * mm, "end": v(-27.15, 11.1) * mm});
            skLineSegment(sketch, "E51.19.13", {"start": v(-23.27, 10.04) * mm, "end": v(-23.6, 10.09) * mm});
            skLineSegment(sketch, "E51.19.14", {"start": v(-23.6, 10.09) * mm, "end": v(-24, 10.12) * mm});
            skLineSegment(sketch, "E51.19.15", {"start": v(-24, 10.12) * mm, "end": v(-24.47, 10.14) * mm});
            skLineSegment(sketch, "E51.19.16", {"start": v(-24.67, 8.38) * mm, "end": v(-25.02, 8.67) * mm});
            skLineSegment(sketch, "E51.19.17", {"start": v(-24.35, 8.14) * mm, "end": v(-24.67, 8.38) * mm});
            skLineSegment(sketch, "E51.19.18", {"start": v(-25.02, 8.67) * mm, "end": v(-25.41, 9.03) * mm});
            skLineSegment(sketch, "E51.19.19", {"start": v(-23, 10) * mm, "end": v(-23.27, 10.04) * mm});
            skLineSegment(sketch, "E51.19.20", {"start": v(-22.8, 9.94) * mm, "end": v(-23, 10) * mm});
            skLineSegment(sketch, "E51.19.21", {"start": v(-24.07, 7.95) * mm, "end": v(-24.35, 8.14) * mm});
            skLineSegment(sketch, "E51.19.22", {"start": v(-23.83, 7.81) * mm, "end": v(-24.07, 7.95) * mm});
            skLineSegment(sketch, "E51.19.23", {"start": v(-23.5, 7.64) * mm, "end": v(-23.64, 7.71) * mm});
            skLineSegment(sketch, "E51.19.24", {"start": v(-22.53, 9.85) * mm, "end": v(-22.56, 9.87) * mm});
            skLineSegment(sketch, "E51.19.25", {"start": v(-22.56, 9.87) * mm, "end": v(-22.65, 9.9) * mm});
            skLineSegment(sketch, "E51.19.26", {"start": v(-23.64, 7.71) * mm, "end": v(-23.83, 7.81) * mm});
            skLineSegment(sketch, "E51.19.27", {"start": v(-22.65, 9.9) * mm, "end": v(-22.8, 9.94) * mm});
            skLineSegment(sketch, "E51.19.28", {"start": v(-23.42, 7.6) * mm, "end": v(-23.5, 7.64) * mm});
            skLineSegment(sketch, "E51.19.29", {"start": v(-23.39, 7.6) * mm, "end": v(-23.42, 7.6) * mm});
            skSolve(sketch);
        }
        {
            var Q0;
            {var subQ0=sQuery(id+"F1.wireOp",EDGE,"E0");var subQ27=makeQuery(id+"F1.imprint","INTERSECT",VERTEX,{"derivedFrom":[subQ0,sQuery(id+"F1.wireOp",EDGE,"E51.10.0")]});Q0=makeQuery(id+"F1.imprint","IMPRINT",FACE,{"disambiguationData":[TD([[makeQuery(id+"F1.imprint","IMPRINT",EDGE,{"disambiguationData":[TD([[subQ27,-1.0]])],"derivedFrom":subQ0}),1.0]])]});}
            var Q1;
            {var subQ0=sQuery(id+"F1.wireOp",EDGE,"E51.1.0");Q1=makeQuery(id+"F1.imprint","IMPRINT",FACE,{"disambiguationData":[TD([[makeQuery(id+"F1.imprint","IMPRINT",EDGE,{"derivedFrom":subQ0}),-1.0]])]});}
            var Q2;
            {var subQ7=sQuery(id+"F1.wireOp",EDGE,"E51.2.0");Q2=makeQuery(id+"F1.imprint","IMPRINT",FACE,{"disambiguationData":[TD([[makeQuery(id+"F1.imprint","IMPRINT",EDGE,{"derivedFrom":subQ7}),-1.0]])]});}
            var Q3;
            {var subQ8=sQuery(id+"F1.wireOp",EDGE,"E51.3.0");Q3=makeQuery(id+"F1.imprint","IMPRINT",FACE,{"disambiguationData":[TD([[makeQuery(id+"F1.imprint","IMPRINT",EDGE,{"derivedFrom":subQ8}),-1.0]])]});}
            var Q4;
            {var subQ2=sQuery(id+"F1.wireOp",EDGE,"E51.4.0");Q4=makeQuery(id+"F1.imprint","IMPRINT",FACE,{"disambiguationData":[TD([[makeQuery(id+"F1.imprint","IMPRINT",EDGE,{"derivedFrom":subQ2}),-1.0]])]});}
            var Q5;
            {var subQ8=sQuery(id+"F1.wireOp",EDGE,"E51.5.0");Q5=makeQuery(id+"F1.imprint","IMPRINT",FACE,{"disambiguationData":[TD([[makeQuery(id+"F1.imprint","IMPRINT",EDGE,{"derivedFrom":subQ8}),-1.0]])]});}
            var Q6;
            {var subQ3=sQuery(id+"F1.wireOp",EDGE,"E51.6.0");Q6=makeQuery(id+"F1.imprint","IMPRINT",FACE,{"disambiguationData":[TD([[makeQuery(id+"F1.imprint","IMPRINT",EDGE,{"derivedFrom":subQ3}),-1.0]])]});}
            var Q7;
            {var subQ0=sQuery(id+"F1.wireOp",EDGE,"E51.7.0");Q7=makeQuery(id+"F1.imprint","IMPRINT",FACE,{"disambiguationData":[TD([[makeQuery(id+"F1.imprint","IMPRINT",EDGE,{"derivedFrom":subQ0}),-1.0]])]});}
            var Q8;
            {var subQ5=sQuery(id+"F1.wireOp",EDGE,"E51.8.0");Q8=makeQuery(id+"F1.imprint","IMPRINT",FACE,{"disambiguationData":[TD([[makeQuery(id+"F1.imprint","IMPRINT",EDGE,{"derivedFrom":subQ5}),-1.0]])]});}
            var Q9;
            {var subQ1=sQuery(id+"F1.wireOp",EDGE,"E51.9.0");Q9=makeQuery(id+"F1.imprint","IMPRINT",FACE,{"disambiguationData":[TD([[makeQuery(id+"F1.imprint","IMPRINT",EDGE,{"derivedFrom":subQ1}),-1.0]])]});}
            var Q10;
            {var subQ5=sQuery(id+"F1.wireOp",EDGE,"E51.10.0");Q10=makeQuery(id+"F1.imprint","IMPRINT",FACE,{"disambiguationData":[TD([[makeQuery(id+"F1.imprint","IMPRINT",EDGE,{"derivedFrom":subQ5}),-1.0]])]});}
            var Q11;
            {var subQ8=sQuery(id+"F1.wireOp",EDGE,"E51.11.0");Q11=makeQuery(id+"F1.imprint","IMPRINT",FACE,{"disambiguationData":[TD([[makeQuery(id+"F1.imprint","IMPRINT",EDGE,{"derivedFrom":subQ8}),-1.0]])]});}
            var Q12;
            {var subQ2=sQuery(id+"F1.wireOp",EDGE,"E51.12.0");Q12=makeQuery(id+"F1.imprint","IMPRINT",FACE,{"disambiguationData":[TD([[makeQuery(id+"F1.imprint","IMPRINT",EDGE,{"derivedFrom":subQ2}),-1.0]])]});}
            var Q13;
            {var subQ3=sQuery(id+"F1.wireOp",EDGE,"E51.13.0");Q13=makeQuery(id+"F1.imprint","IMPRINT",FACE,{"disambiguationData":[TD([[makeQuery(id+"F1.imprint","IMPRINT",EDGE,{"derivedFrom":subQ3}),-1.0]])]});}
            var Q14;
            {var subQ0=sQuery(id+"F1.wireOp",EDGE,"E51.14.0");Q14=makeQuery(id+"F1.imprint","IMPRINT",FACE,{"disambiguationData":[TD([[makeQuery(id+"F1.imprint","IMPRINT",EDGE,{"derivedFrom":subQ0}),-1.0]])]});}
            var Q15;
            {var subQ6=sQuery(id+"F1.wireOp",EDGE,"E51.15.0");Q15=makeQuery(id+"F1.imprint","IMPRINT",FACE,{"disambiguationData":[TD([[makeQuery(id+"F1.imprint","IMPRINT",EDGE,{"derivedFrom":subQ6}),-1.0]])]});}
            var Q16;
            {var subQ5=sQuery(id+"F1.wireOp",EDGE,"E51.16.0");Q16=makeQuery(id+"F1.imprint","IMPRINT",FACE,{"disambiguationData":[TD([[makeQuery(id+"F1.imprint","IMPRINT",EDGE,{"derivedFrom":subQ5}),-1.0]])]});}
            var Q17;
            {var subQ7=sQuery(id+"F1.wireOp",EDGE,"E51.17.0");Q17=makeQuery(id+"F1.imprint","IMPRINT",FACE,{"disambiguationData":[TD([[makeQuery(id+"F1.imprint","IMPRINT",EDGE,{"derivedFrom":subQ7}),-1.0]])]});}
            var Q18;
            {var subQ5=sQuery(id+"F1.wireOp",EDGE,"E51.18.0");Q18=makeQuery(id+"F1.imprint","IMPRINT",FACE,{"disambiguationData":[TD([[makeQuery(id+"F1.imprint","IMPRINT",EDGE,{"derivedFrom":subQ5}),-1.0]])]});}
            var Q19;
            {var subQ8=sQuery(id+"F1.wireOp",EDGE,"E51.19.0");Q19=makeQuery(id+"F1.imprint","IMPRINT",FACE,{"disambiguationData":[TD([[makeQuery(id+"F1.imprint","IMPRINT",EDGE,{"derivedFrom":subQ8}),-1.0]])]});}
            var Q20;
            {var subQ8=sQuery(id+"F1.wireOp",EDGE,"E21");Q20=makeQuery(id+"F1.imprint","IMPRINT",FACE,{"disambiguationData":[TD([[makeQuery(id+"F1.imprint","IMPRINT",EDGE,{"derivedFrom":subQ8}),-1.0]])]});}
            extrude(context, id + "F2", {"entities" : qUnion([Q0, Q1, Q2, Q3, Q4, Q5, Q6, Q7, Q8, Q9, Q10, Q11, Q12, Q13, Q14, Q15, Q16, Q17, Q18, Q19, Q20]), "depth" : (getVariable(context, 'GearThickness')) * mm});
        }
    });
